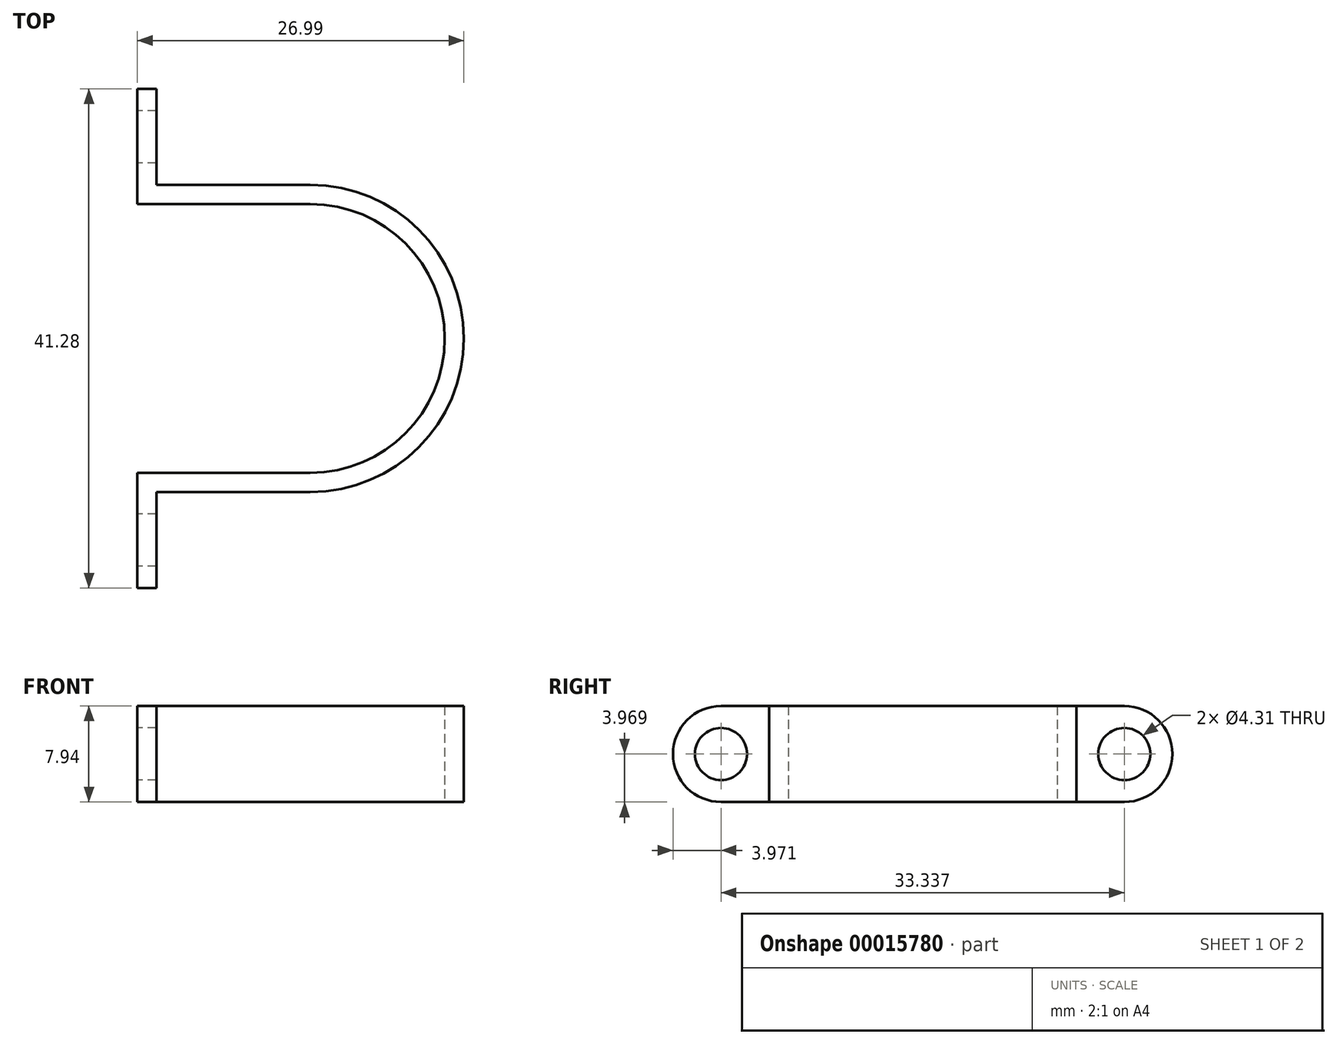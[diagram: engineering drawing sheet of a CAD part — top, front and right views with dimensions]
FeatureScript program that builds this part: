
annotation { "Feature Type Name" : "Feature", "Feature Type Description" : "" }
export const myFeature = defineFeature(function(context is Context, id is Id, definition is map)
    precondition{}
    {
        {
            var Q0;
            Q0=qCreatedBy(makeId("Top.planeOp"),FACE);
            var sketch = newSketch(context, id + "F0", { "sketchPlane" : qUnion([Q0])});
            skArc(sketch, "E0", {"start": v(0, -12.7) * mm, "mid": v(12.7, 0) * mm, "end": v(0, 12.7) * mm});
            skLineSegment(sketch, "E1", {"start": v(0, 12.7) * mm, "end": v(-12.7, 12.7) * mm});
            skLineSegment(sketch, "E2", {"start": v(0, -12.7) * mm, "end": v(-12.7, -12.7) * mm});
            skLineSegment(sketch, "E3", {"start": v(-12.7, -12.7) * mm, "end": v(-12.7, -20.64) * mm});
            skLineSegment(sketch, "E4", {"start": v(-12.7, -20.64) * mm, "end": v(-14.29, -20.64) * mm});
            skLineSegment(sketch, "E5", {"start": v(-14.29, 20.64) * mm, "end": v(-12.7, 20.64) * mm});
            skLineSegment(sketch, "E6", {"start": v(-12.7, 20.64) * mm, "end": v(-12.7, 12.7) * mm});
            skLineSegment(sketch, "E7", {"start": v(0, 12.7) * mm, "end": v(0, 11.11) * mm, "construction": true});
            skLineSegment(sketch, "E8", {"start": v(0, 11.11) * mm, "end": v(0, -11.11) * mm, "construction": true});
            skLineSegment(sketch, "E9", {"start": v(0, -11.11) * mm, "end": v(0, -12.7) * mm, "construction": true});
            skArc(sketch, "E10", {"start": v(0, -11.11) * mm, "mid": v(11.11, 0) * mm, "end": v(0, 11.11) * mm});
            skLineSegment(sketch, "E11", {"start": v(0, -11.11) * mm, "end": v(-14.29, -11.11) * mm});
            skLineSegment(sketch, "E12", {"start": v(-14.29, -11.11) * mm, "end": v(-14.29, -20.64) * mm});
            skLineSegment(sketch, "E13", {"start": v(0, 11.11) * mm, "end": v(-14.29, 11.11) * mm});
            skLineSegment(sketch, "E14", {"start": v(-14.29, 11.11) * mm, "end": v(-14.29, 20.64) * mm});
            skLineSegment(sketch, "E15", {"start": v(0, 0) * mm, "end": v(-14.29, 0) * mm, "construction": true});
            skLineSegment(sketch, "E16", {"start": v(-14.29, 11.11) * mm, "end": v(-14.29, -11.11) * mm, "construction": true});
            skSolve(sketch);
        }
        {
            var Q0;
            Q0=qSketchRegion(id+"F0",true);
            extrude(context, id + "F1", {"entities" : qUnion([Q0]), "depth" : 7.94 * mm});
        }
        {
            var Q0;
            Q0=makeQuery(id+"F1.opExtrude","CAP_EDGE",EDGE,{"disambiguationData":[OSD([sQuery(id+"F0.wireOp",EDGE,"E5")])],"isStart":false});
            var Q1;
            Q1=makeQuery(id+"F1.opExtrude","CAP_EDGE",EDGE,{"disambiguationData":[OSD([sQuery(id+"F0.wireOp",EDGE,"E5")])],"isStart":true});
            var Q2;
            Q2=makeQuery(id+"F1.opExtrude","CAP_EDGE",EDGE,{"disambiguationData":[OSD([sQuery(id+"F0.wireOp",EDGE,"E4")])],"isStart":false});
            var Q3;
            Q3=makeQuery(id+"F1.opExtrude","CAP_EDGE",EDGE,{"disambiguationData":[OSD([sQuery(id+"F0.wireOp",EDGE,"E4")])],"isStart":true});
            fillet(context, id + "F2", {"entities" : qUnion([Q0, Q1, Q2, Q3]), "radius" : 3.97 * mm, "tangentPropagation" : true, "allowEdgeOverflow" : false});
        }
        {
            var Q0;
            Q0=makeQuery(id+"F1.opExtrude","SWEPT_FACE",FACE,{"disambiguationData":[OSD([sQuery(id+"F0.wireOp",EDGE,"E14")])]});
            var sketch = newSketch(context, id + "F3", { "sketchPlane" : qUnion([Q0])});
            skCircle(sketch, "E17", {"center": v(-16.67, 3.97) * mm, "radius": 2.15 * mm});
            skCircle(sketch, "E18", {"center": v(16.67, 3.97) * mm, "radius": 2.15 * mm});
            skSolve(sketch);
        }
        {
            var Q0;
            Q0 = qSketchRegion(id + "F3", true);
            var Q1;
            Q1=makeQuery(id+"F1.opExtrude","SWEPT_FACE",FACE,{"disambiguationData":[OSD([sQuery(id+"F0.wireOp",EDGE,"E6")])]});
            extrude(context, id + "F4", {"entities" : qUnion([Q0]), "operationType" : NewBodyOperationType.REMOVE, "endBound" : BoundingType.UP_TO_SURFACE, "oppositeDirection" : true, "endBoundEntityFace" : qUnion([Q1]), "depth" : 25.4 * mm});
        }
    });
